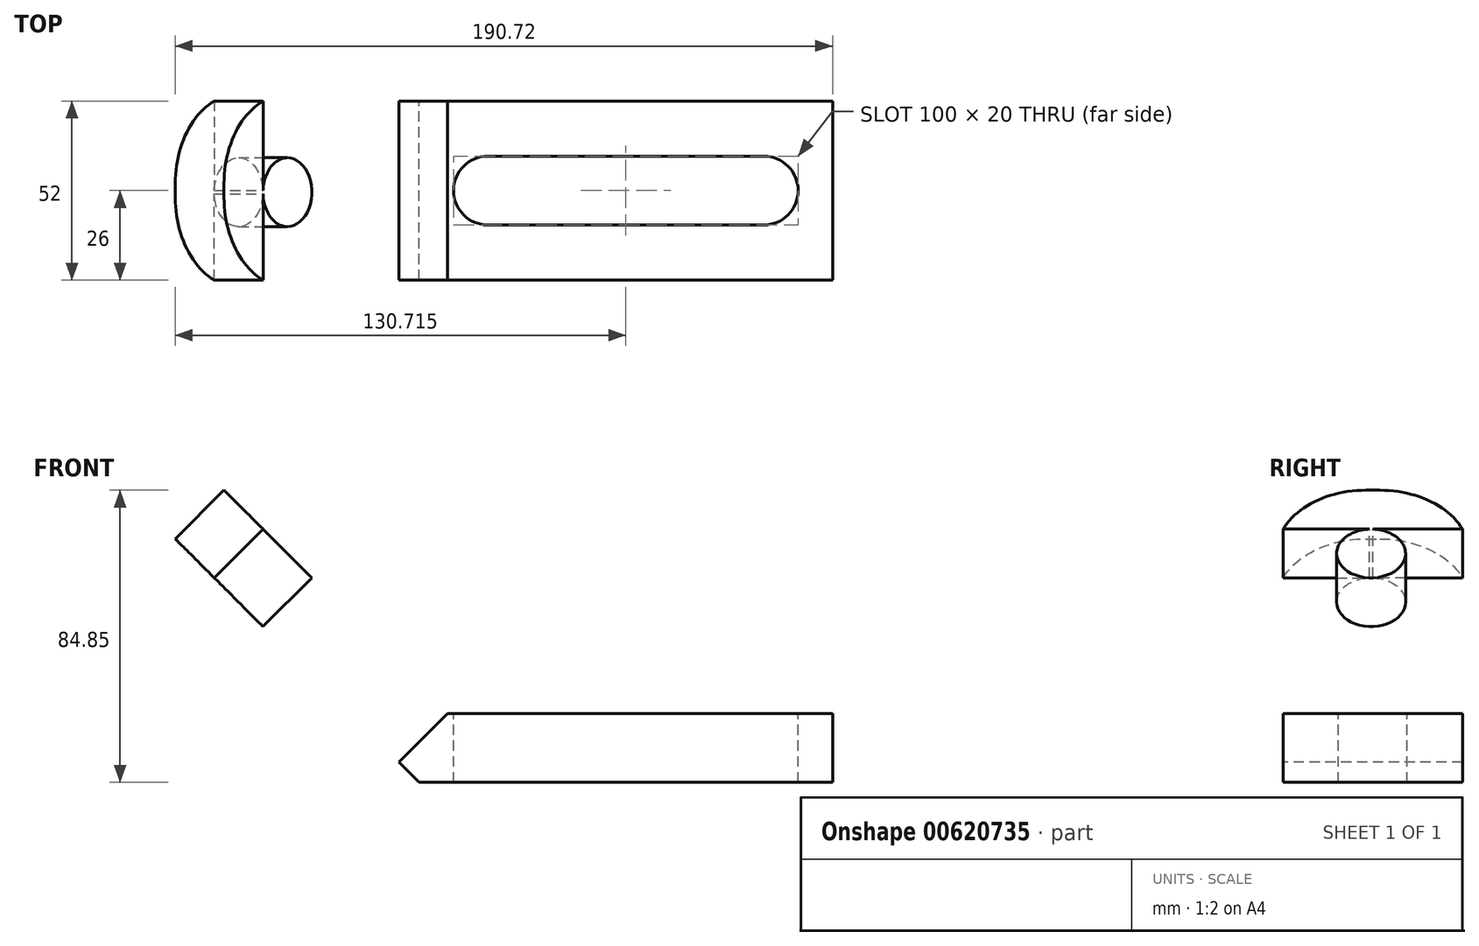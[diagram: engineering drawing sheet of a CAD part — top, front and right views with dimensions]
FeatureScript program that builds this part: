
annotation { "Feature Type Name" : "Feature", "Feature Type Description" : "" }
export const myFeature = defineFeature(function(context is Context, id is Id, definition is map)
    precondition{}
    {
        {
            var Q0;
            Q0=qCreatedBy(makeId("Front.planeOp"),FACE);
            var sketch = newSketch(context, id + "F0", { "sketchPlane" : qUnion([Q0])});
            skLineSegment(sketch, "E0.bottom", {"start": v(-38.25, 0) * mm, "end": v(81.75, 0) * mm});
            skLineSegment(sketch, "E0.top", {"start": v(-38.25, -20) * mm, "end": v(81.75, -20) * mm});
            skLineSegment(sketch, "E0.left", {"start": v(-38.25, 0) * mm, "end": v(-38.25, -20) * mm});
            skLineSegment(sketch, "E0.right", {"start": v(81.75, 0) * mm, "end": v(81.75, -20) * mm});
            skLineSegment(sketch, "E1.bottom", {"start": v(-38.25, 0) * mm, "end": v(-35.53, 0) * mm});
            skLineSegment(sketch, "E1.top", {"start": v(-38.25, -20) * mm, "end": v(-38.25, -20) * mm});
            skLineSegment(sketch, "E2", {"start": v(-38.25, -20) * mm, "end": v(-108.97, 50.71) * mm});
            skLineSegment(sketch, "E3", {"start": v(-108.97, 50.71) * mm, "end": v(-94.82, 64.85) * mm});
            skLineSegment(sketch, "E4", {"start": v(-94.82, 64.85) * mm, "end": v(-9.97, -20) * mm});
            skSolve(sketch);
        }
        {
            var Q0;
            Q0 = qSketchRegion(id + "F0", true);
            extrude(context, id + "F1", {"entities" : qUnion([Q0]), "depth" : 52 * mm, "offsetDistance" : 25 * mm});
        }
        {
            var Q0;
            Q0=makeQuery(id+"F1.opExtrude","SWEPT_FACE",FACE,{"disambiguationData":[OSD([sQuery(id+"F0.wireOp",EDGE,"E0.bottom"),sQuery(id+"F0.wireOp",EDGE,"E1.bottom")])]});
            var sketch = newSketch(context, id + "F2", { "sketchPlane" : qUnion([Q0])});
            skLineSegment(sketch, "E5", {"start": v(71.75, 0) * mm, "end": v(71.75, -52) * mm});
            skPoint(sketch, "E6.middle", {"position": v(0, -26) * mm});
            skArc(sketch, "E7", {"start": v(61.75, -36) * mm, "mid": v(71.75, -26) * mm, "end": v(61.75, -16) * mm});
            skLineSegment(sketch, "E8", {"start": v(61.75, -16) * mm, "end": v(-18.25, -16) * mm});
            skLineSegment(sketch, "E9", {"start": v(61.75, -36) * mm, "end": v(-18.25, -36) * mm});
            skArc(sketch, "E10", {"start": v(-18.25, -16) * mm, "mid": v(-28.25, -26) * mm, "end": v(-18.25, -36) * mm});
            skSolve(sketch);
        }
        {
            var Q0;
            Q0 = qSketchRegion(id + "F2", true);
            extrude(context, id + "F3", {"entities" : qUnion([Q0]), "operationType" : NewBodyOperationType.REMOVE, "oppositeDirection" : true, "depth" : 20 * mm, "offsetDistance" : 25 * mm});
        }
        {
            var Q0;
            Q0=makeQuery(id+"F1.opExtrude","SWEPT_FACE",FACE,{"disambiguationData":[OSD([sQuery(id+"F0.wireOp",EDGE,"E4")])]});
            var sketch = newSketch(context, id + "F4", { "sketchPlane" : qUnion([Q0])});
            skLineSegment(sketch, "E11", {"start": v(-26, 112.9) * mm, "end": v(-26, 96.9) * mm});
            skLineSegment(sketch, "E12", {"start": v(-26, 96.9) * mm, "end": v(-52, 96.9) * mm});
            skLineSegment(sketch, "E13", {"start": v(-52, 96.9) * mm, "end": v(0, 96.9) * mm});
            skCircle(sketch, "E14", {"center": v(-26.5, 86.92) * mm, "radius": 10 * mm});
            skSolve(sketch);
        }
        {
            var Q0;
            {var subQ0=sQuery(id+"F4.wireOp",EDGE,"E14");var subQ1=sQuery(id+"F4.wireOp",EDGE,"E13");var subQ3=makeQuery(id+"F4.imprint","INTERSECT",VERTEX,{"derivedFrom":[subQ1,subQ0]});Q0=makeQuery(id+"F4.imprint","IMPRINT",FACE,{"disambiguationData":[TD([[makeQuery(id+"F4.imprint","IMPRINT",EDGE,{"disambiguationData":[TD([[subQ3,-1.0]])],"derivedFrom":subQ1}),-1.0]])]});}
            extrude(context, id + "F5", {"entities" : qUnion([Q0]), "operationType" : NewBodyOperationType.REMOVE, "oppositeDirection" : true, "depth" : 25 * mm, "offsetDistance" : 25 * mm});
        }
        {
            var Q0;
            Q0=makeQuery(id+"F1.opExtrude","CAP_EDGE",EDGE,{"disambiguationData":[OSD([sQuery(id+"F0.wireOp",EDGE,"E3")])],"isStart":false});
            fillet(context, id + "F6", {"entities" : qUnion([Q0]), "radius" : 26 * mm, "tangentPropagation" : true, "allowEdgeOverflow" : false});
        }
        {
            var Q0;
            Q0=makeQuery(id+"F1.opExtrude","CAP_EDGE",EDGE,{"disambiguationData":[OSD([sQuery(id+"F0.wireOp",EDGE,"E3")])],"isStart":true});
            fillet(context, id + "F7", {"entities" : qUnion([Q0]), "radius" : 26 * mm, "tangentPropagation" : true, "allowEdgeOverflow" : false});
        }
    });
